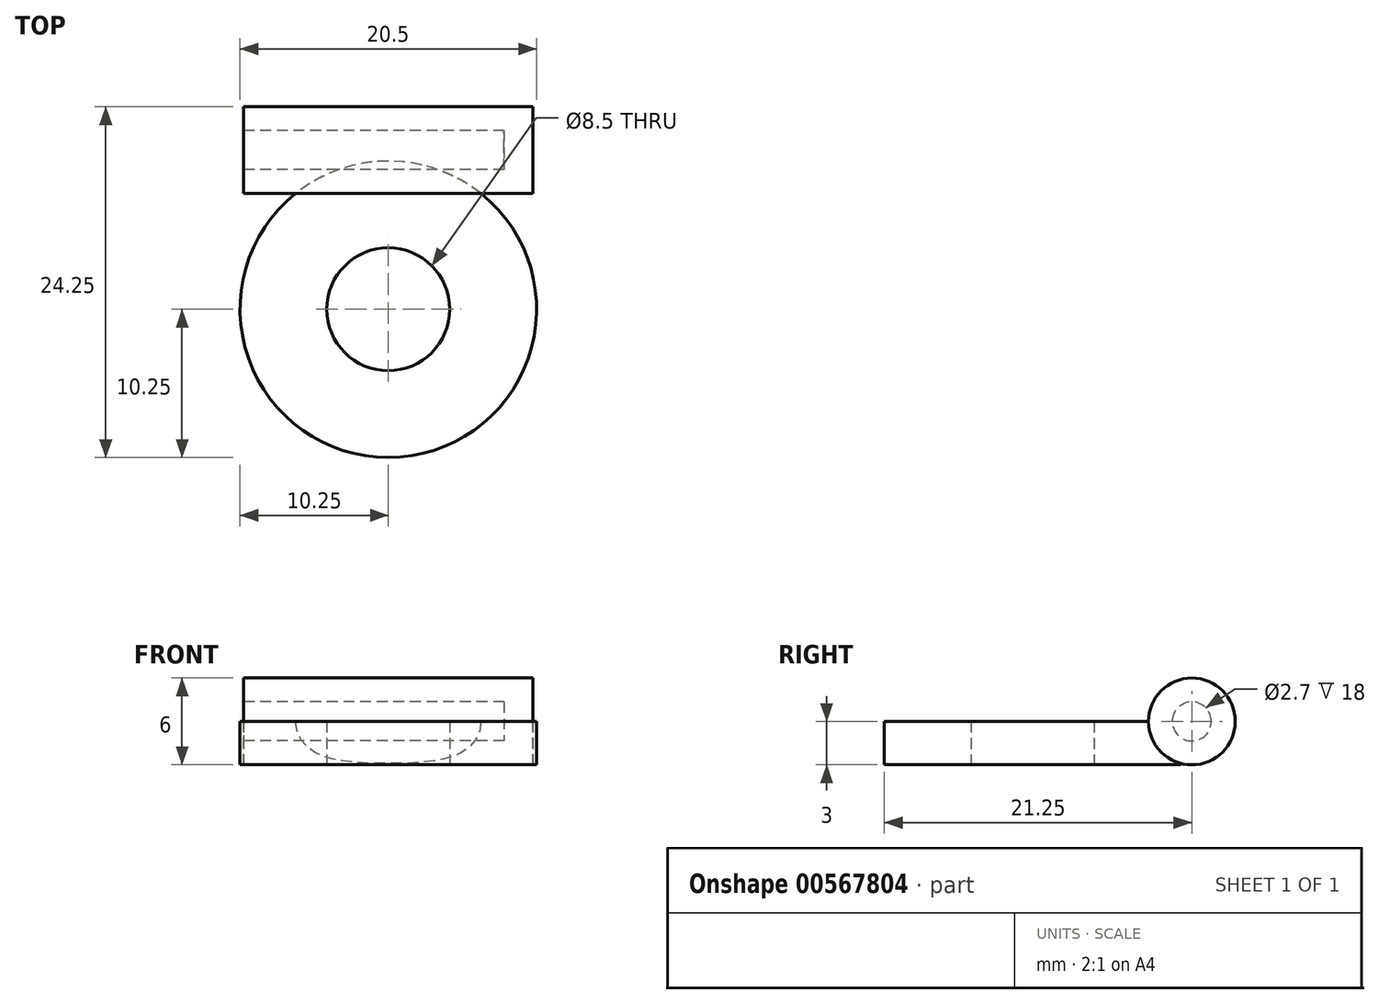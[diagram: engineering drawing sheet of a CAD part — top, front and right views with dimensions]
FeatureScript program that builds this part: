
annotation { "Feature Type Name" : "Feature", "Feature Type Description" : "" }
export const myFeature = defineFeature(function(context is Context, id is Id, definition is map)
    precondition{}
    {
        {
            var Q0;
            Q0=qCreatedBy(makeId("Top.planeOp"),FACE);
            var sketch = newSketch(context, id + "F0", { "sketchPlane" : qUnion([Q0])});
            skCircle(sketch, "E0", {"center": v(0, 0) * mm, "radius": 4.25 * mm});
            skCircle(sketch, "E1.0", {"center": v(0, 0) * mm, "radius": 10.25 * mm});
            skSolve(sketch);
        }
        {
            var Q0;
            Q0=makeQuery(id+"F0.imprint","IMPRINT",FACE,{"disambiguationData":[TD([[makeQuery(id+"F0.imprint","IMPRINT",EDGE,{"derivedFrom":sQuery(id+"F0.wireOp",EDGE,"E0")}),-1.0]])]});
            extrude(context, id + "F1", {"entities" : qUnion([Q0]), "depth" : 3 * mm, "offsetDistance" : 25 * mm});
        }
        {
            var Q0;
            Q0=qCreatedBy(makeId("Right.planeOp"),FACE);
            var sketch = newSketch(context, id + "F2", { "sketchPlane" : qUnion([Q0])});
            skCircle(sketch, "E2", {"center": v(11, 3) * mm, "radius": 3 * mm});
            skSolve(sketch);
        }
        {
            var Q0;
            Q0=makeQuery(id+"F2.imprint","IMPRINT",FACE,{"disambiguationData":[TD([[makeQuery(id+"F2.imprint","IMPRINT",EDGE,{"derivedFrom":sQuery(id+"F2.wireOp",EDGE,"E2")}),1.0]])]});
            extrude(context, id + "F3", {"entities" : qUnion([Q0]), "operationType" : NewBodyOperationType.ADD, "depth" : 10 * mm, "offsetDistance" : 25 * mm, "hasSecondDirection" : true, "secondDirectionOppositeDirection" : true, "secondDirectionDepth" : 10 * mm});
        }
        {
            var Q0;
            Q0=makeQuery(id+"F3.opExtrude","CAP_FACE",FACE,{"disambiguationData":[OSD([sQuery(id+"F2.wireOp",EDGE,"E2")])],"isStart":true});
            var sketch = newSketch(context, id + "F4", { "sketchPlane" : qUnion([Q0])});
            skCircle(sketch, "E3", {"center": v(-11, 3) * mm, "radius": 1.35 * mm});
            skSolve(sketch);
        }
        {
            var Q0;
            Q0=makeQuery(id+"F4.imprint","IMPRINT",FACE,{"disambiguationData":[TD([[makeQuery(id+"F4.imprint","IMPRINT",EDGE,{"derivedFrom":sQuery(id+"F4.wireOp",EDGE,"E3")}),1.0]])]});
            extrude(context, id + "F5", {"entities" : qUnion([Q0]), "operationType" : NewBodyOperationType.REMOVE, "oppositeDirection" : true, "depth" : 18 * mm, "offsetDistance" : 25 * mm});
        }
    });
